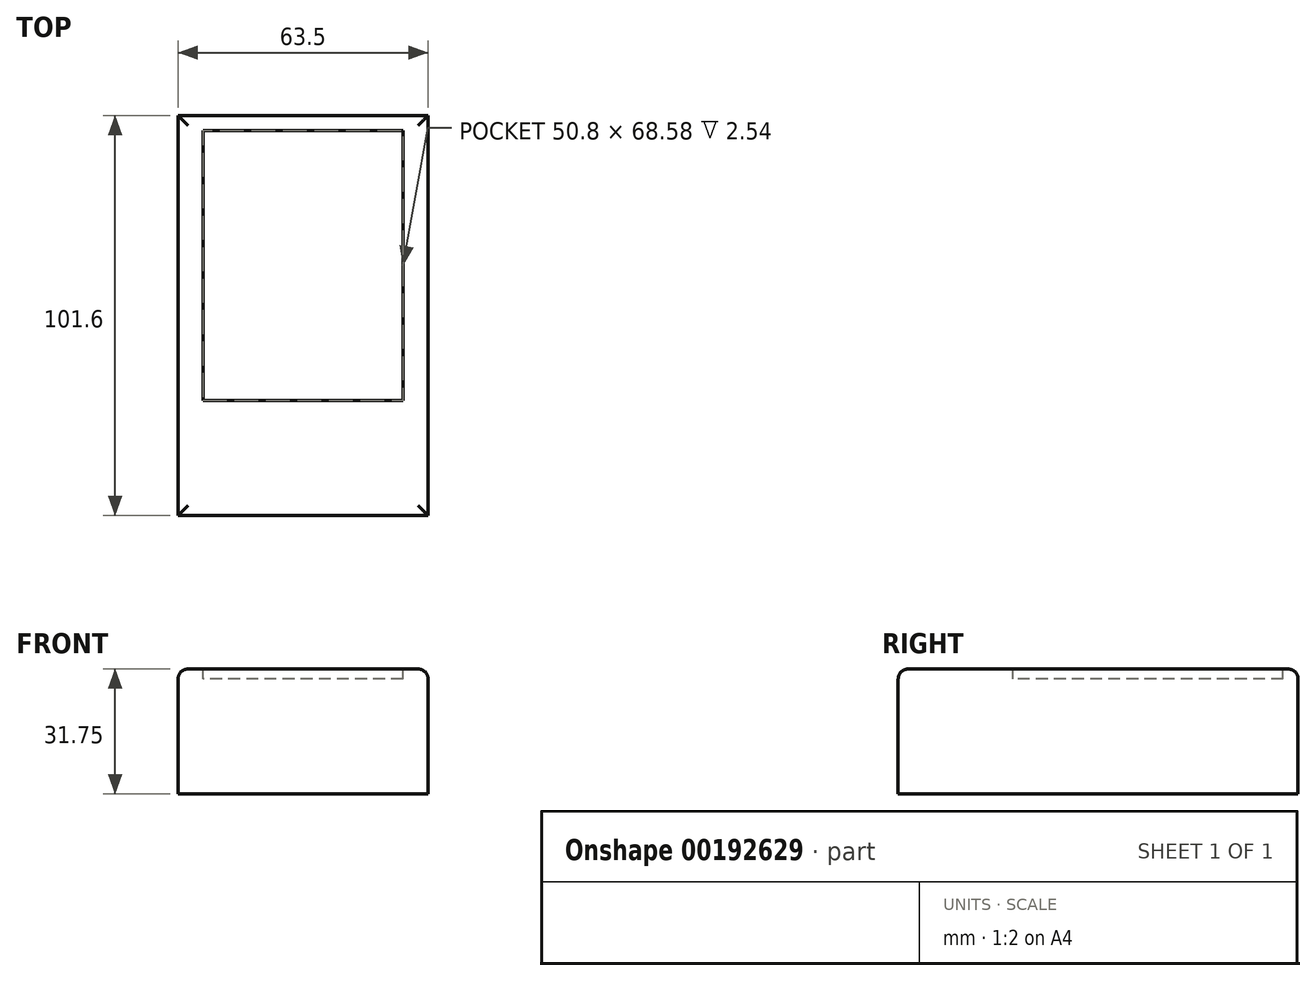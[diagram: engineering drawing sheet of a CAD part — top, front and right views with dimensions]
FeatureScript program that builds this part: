
annotation { "Feature Type Name" : "Feature", "Feature Type Description" : "" }
export const myFeature = defineFeature(function(context is Context, id is Id, definition is map)
    precondition{}
    {
        {
            var Q0;
            Q0=qCreatedBy(makeId("Top.planeOp"),FACE);
            var sketch = newSketch(context, id + "F0", { "sketchPlane" : qUnion([Q0])});
            skLineSegment(sketch, "E0.bottom", {"start": v(31.75, 50.8) * mm, "end": v(-31.75, 50.8) * mm});
            skLineSegment(sketch, "E0.top", {"start": v(31.75, -50.8) * mm, "end": v(-31.75, -50.8) * mm});
            skLineSegment(sketch, "E0.left", {"start": v(31.75, 50.8) * mm, "end": v(31.75, -50.8) * mm});
            skLineSegment(sketch, "E0.right", {"start": v(-31.75, 50.8) * mm, "end": v(-31.75, -50.8) * mm});
            skPoint(sketch, "E0.middle", {"position": v(0, 0) * mm});
            skSolve(sketch);
        }
        {
            var Q0;
            Q0=makeQuery(id+"F0.imprint","IMPRINT",FACE,{"disambiguationData":[TD([[makeQuery(id+"F0.imprint","IMPRINT",EDGE,{"derivedFrom":sQuery(id+"F0.wireOp",EDGE,"E0.bottom")}),1.0]])]});
            extrude(context, id + "F1", {"entities" : qUnion([Q0]), "depth" : 31.75 * mm});
        }
        {
            var Q0;
            Q0=makeQuery(id+"F1.opExtrude","CAP_EDGE",EDGE,{"disambiguationData":[OSD([sQuery(id+"F0.wireOp",EDGE,"E0.bottom")])],"isStart":false});
            var Q1;
            Q1=makeQuery(id+"F1.opExtrude","CAP_EDGE",EDGE,{"disambiguationData":[OSD([sQuery(id+"F0.wireOp",EDGE,"E0.right")])],"isStart":false});
            var Q2;
            Q2=makeQuery(id+"F1.opExtrude","CAP_EDGE",EDGE,{"disambiguationData":[OSD([sQuery(id+"F0.wireOp",EDGE,"E0.left")])],"isStart":false});
            var Q3;
            Q3=makeQuery(id+"F1.opExtrude","CAP_EDGE",EDGE,{"disambiguationData":[OSD([sQuery(id+"F0.wireOp",EDGE,"E0.top")])],"isStart":false});
            fillet(context, id + "F2", {"entities" : qUnion([Q0, Q1, Q2, Q3]), "radius" : 2.54 * mm, "tangentPropagation" : true, "allowEdgeOverflow" : false});
        }
        {
            var Q0;
            Q0=makeQuery(id+"F1.opExtrude","CAP_FACE",FACE,{"disambiguationData":[OSD([sQuery(id+"F0.wireOp",EDGE,"E0.bottom"),sQuery(id+"F0.wireOp",EDGE,"E0.top"),sQuery(id+"F0.wireOp",EDGE,"E0.left"),sQuery(id+"F0.wireOp",EDGE,"E0.right")])],"isStart":false});
            var sketch = newSketch(context, id + "F3", { "sketchPlane" : qUnion([Q0])});
            skLineSegment(sketch, "E1.bottom", {"start": v(25.4, 47) * mm, "end": v(-25.4, 47) * mm});
            skLineSegment(sketch, "E1.top", {"start": v(25.4, -21.6) * mm, "end": v(-25.4, -21.6) * mm});
            skLineSegment(sketch, "E1.left", {"start": v(25.4, 47) * mm, "end": v(25.4, -21.6) * mm});
            skLineSegment(sketch, "E1.right", {"start": v(-25.4, 47) * mm, "end": v(-25.4, -21.59) * mm});
            skPoint(sketch, "E1.middle", {"position": v(0, 12.7) * mm});
            skSolve(sketch);
        }
        {
            var Q0;
            Q0=makeQuery(id+"F3.imprint","IMPRINT",FACE,{"disambiguationData":[TD([[makeQuery(id+"F3.imprint","IMPRINT",EDGE,{"derivedFrom":sQuery(id+"F3.wireOp",EDGE,"E1.bottom")}),1.0]])]});
            extrude(context, id + "F4", {"entities" : qUnion([Q0]), "operationType" : NewBodyOperationType.REMOVE, "oppositeDirection" : true, "depth" : 2.54 * mm});
        }
    });
